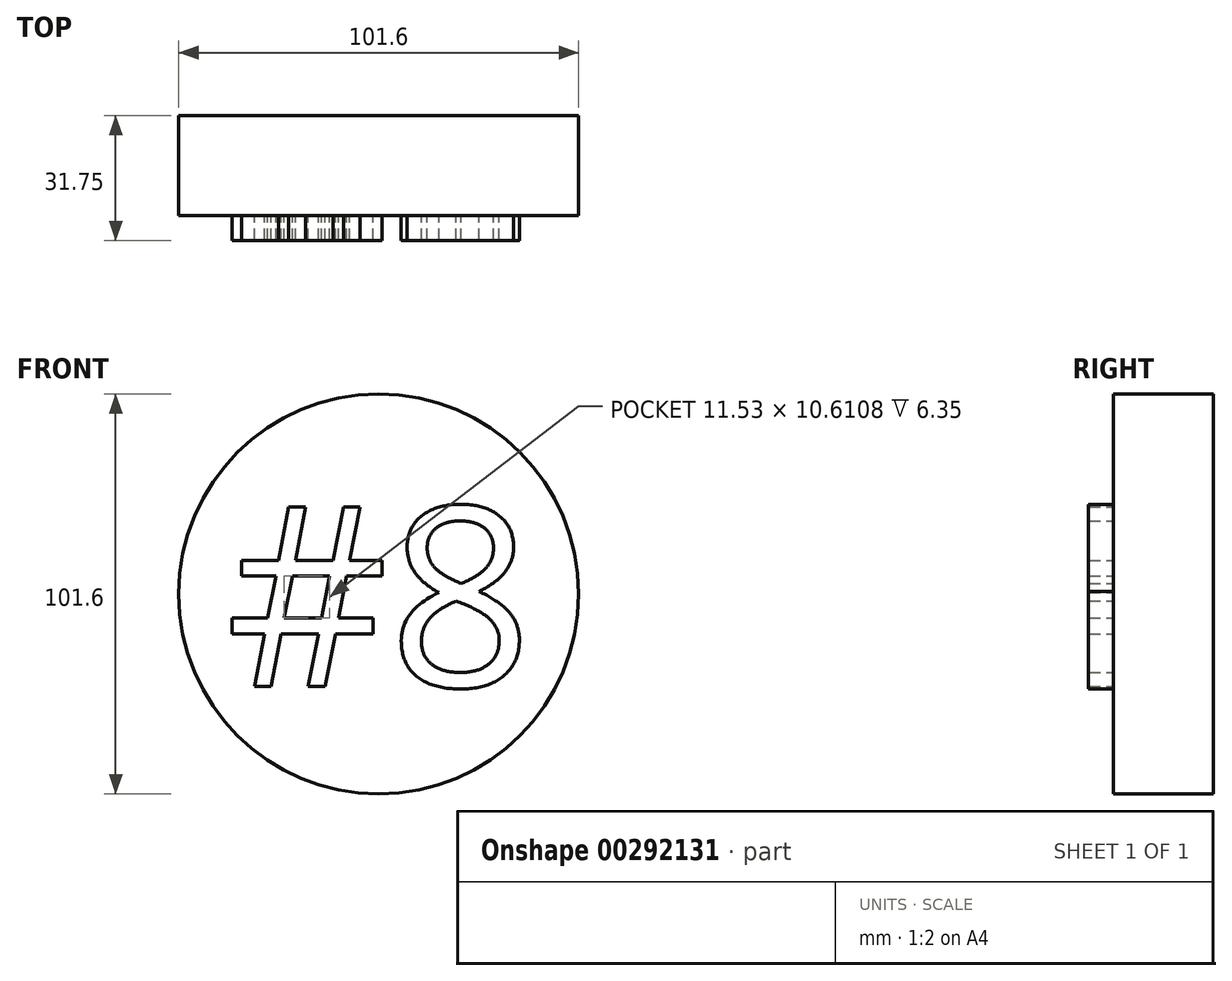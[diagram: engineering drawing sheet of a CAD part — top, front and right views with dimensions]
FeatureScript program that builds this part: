
annotation { "Feature Type Name" : "Feature", "Feature Type Description" : "" }
export const myFeature = defineFeature(function(context is Context, id is Id, definition is map)
    precondition{}
    {
        {
            var Q0;
            Q0=qCreatedBy(makeId("Front.planeOp"),FACE);
            var sketch = newSketch(context, id + "F0", { "sketchPlane" : qUnion([Q0])});
            skCircle(sketch, "E0", {"center": v(0, 0) * mm, "radius": 50.8 * mm});
            skSolve(sketch);
        }
        {
            var Q0;
            Q0 = qSketchRegion(id + "F0", true);
            extrude(context, id + "F1", {"entities" : qUnion([Q0]), "depth" : 25.4 * mm});
        }
        {
            var Q0;
            Q0=makeQuery(id+"F1.opExtrude","CAP_FACE",FACE,{"disambiguationData":[OSD([sQuery(id+"F0.wireOp",EDGE,"E0")])],"isStart":false});
            var sketch = newSketch(context, id + "F2", { "sketchPlane" : qUnion([Q0])});
            skText(sketch, "E1", { "text": "#8", "fontName": "OpenSans-Regular.ttf"});
            const initialGuessF2  = {"E1": [-0.03882, -0.02352, 1, 0, 0.04604]};
            skSetInitialGuess(sketch, initialGuessF2);
            skSolve(sketch);
        }
        {
            var Q0;
            Q0 = qSketchRegion(id + "F2", true);
            extrude(context, id + "F3", {"entities" : qUnion([Q0]), "operationType" : NewBodyOperationType.ADD, "depth" : 6.35 * mm});
        }
    });
